# Revit family: VT.383.B.05
name_source: partatom
category: Оборудование
units: mm (PartAtom-declared; Revit-internal decimal feet)

## family parameters
Всегда вертикально = Да
Заголовок OmniClass = Climate Control (HVAC)
На основе рабочей плоскости = Нет
Номер OmniClass = 23.75.00.00
Общий = Нет
При загрузке вырезать с полостями = Нет
Размер круглого соединителя = Использовать диаметр
Тип детали = Нормальный
Точка расчета площади = Нет

## types (2) — shared parameters
BIM категория объекта = Дополнительный
дополнительный
Дополнительный
DN = 20 мм
EMCS Версия = 3.0
IFC классификация = Клапан
Revit Version = 2018
URL = https://valtec.ru
Uniclass 1.4 Описание = Водопроводные системы
Uniclass 2015 имя = Водопроводные системы
Uniformat II Описание = HVAC
url продукта = https://valtec.ru
Версия = Rev.00
Вес = 0.61 кг
Вес нетто (Kg) = 0
Группа модели = ДЕШЛАМАТОРЫ®
Жидкости применения = Вода и раствор гликоля
Изготовитель = IVAR
Инструкции по установке = https://valtec.ru
Комментарии к типоразмеру = Разработано в Италии
Макс рабочая температура (°C) = 90 °C
Макс рабочее давление (bar) = 3 бары
Максимальный процент гликоля (%) = 50
Максимальный расход (m3/h) = 1.5 м³/ч
Мастерформат 2014 Описание = Отопление, вентиляция и кондиционирование воздуха (HVAC)
Материал основной = Polyamide
Минимальная рабочая температура (°C) = 0 °C
Название производителя = IVAR
Описание = Поворотный магнитный грязеуловитель с фильтром
Описание статьи = Поворотный магнитный грязеуловитель с фильтром
Произведено в = Сделано в Италии
Производитель URL = https://valtec.ru
Размер соединения = 3/4"
Страна производитель = Italy
Техническое описание = https://valtec.ru
Тип соединения = Gas ISO 228/1
zero-valued in all types: Номинальная высота, Номинальная ширина

## per-type parameters (varying)
| type | BIM главная категория объекта | BIM код категории объекта | BIM код основной категории объекта | NBS Описание | Uniclass 2.0 Описание | Группа товаров | Марка url | Материал | Описание OmniClass | Описание Конфигурации | Отделка Белый | Отделка серый | Практическое руководство по использованию семьи | Семейство продуктов |
| RAL7016 | Водопровод | Водопроводным-другой | Водопровод | Клапаны | Клапаны | Дополнительный | http://www.ivar-group.com | Techno-Polymer RAL7016 | Клапаны | Фильтрация гарантируется во всех 4 доступных конфигурациях благодаря поворотной вставке (заявка на патент подана), которая заставляет поток воды внутри фильтра, который задерживает загрязнения. | Нет | Да | Фильтрация гарантируется во всех 4 доступных конфигурациях благодаря поворотной вставке (ожидается получение патента). Поворотная вставка заставляет поток воды внутри сетчатого фильтра, который задерживает загрязнения.
- Вы можете выбрать одну из 4 конфигураций: «Компоновка A» или «Компоновка A1» или «Компоновка B» или «Компоновка B1». Отметьте эту опцию в параметре «Свойства модели - макет». Будьте осторожны: вы должны выбрать только один макет.
- Вы можете выбрать один из двух дополнительных комплектов. Отметьте эту опцию в параметре «Свойства модели - Комплект с дополнительными присадками HT (высокотемпературная система)» или «Комплект с дополнительными присадками LT (низкотемпературная система)». Будьте осторожны: вы должны выбрать только один дополнительный комплект.
- Вы можете выбрать между двумя различными отделками. Отметьте эту опцию в параметре «Модели и отделка - Отделка серого или Отделка белого» | Дополнительный |
| RAL9010 | Plumbing | водопроводным-дополнительный
дополнительный
Дополнительный | водопровод | Арматура | Арматура | Дополнительный
дополнительный
Дополнительный | https://valtec.ru | Techno-Polymer RAL9010 | Арматура | Фильтрация гарантируется во всех 4 доступных конфигурациях благодаря поворотной вставке (ожидается получение патента)
это заставляет поток воды внутри фильтра, который задерживает примеси. | Да | Нет |  | Дополнительный
дополнительный
Дополнительный |

## geometry (parser evidence)
native form markers: Sweep x3
no freeform markers — native parametric forms only
